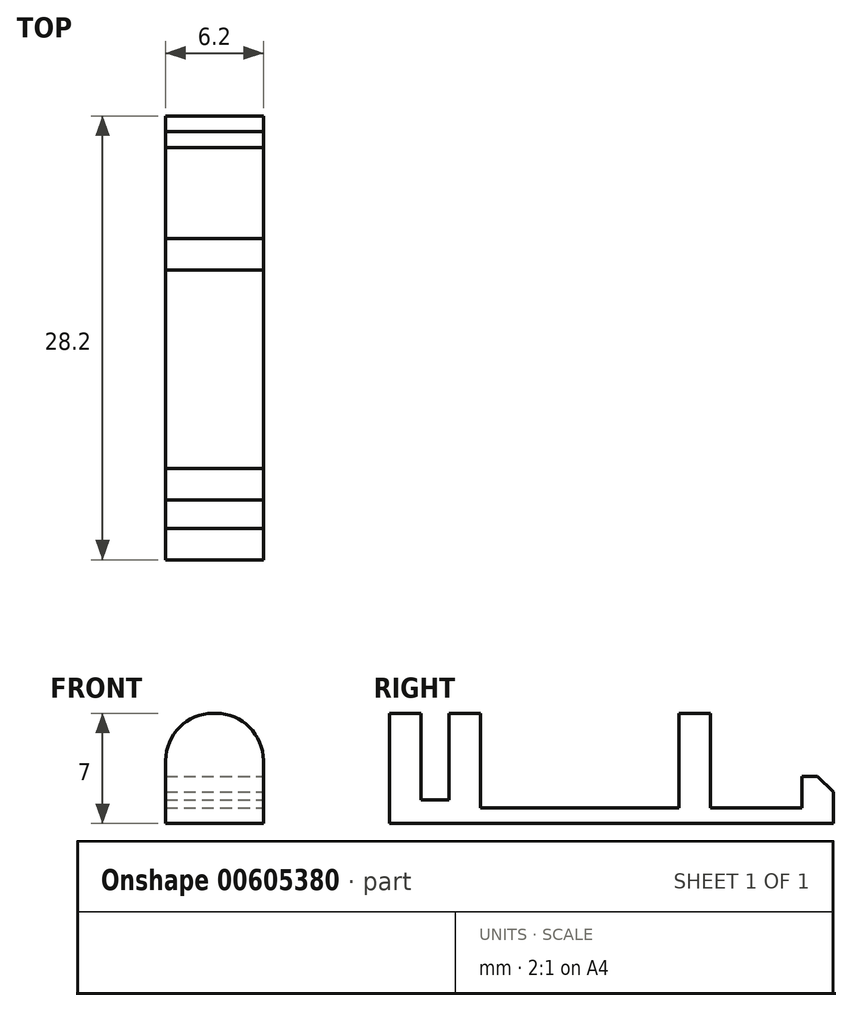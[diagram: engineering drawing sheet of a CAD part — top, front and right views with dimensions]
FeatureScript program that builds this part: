
annotation { "Feature Type Name" : "Feature", "Feature Type Description" : "" }
export const myFeature = defineFeature(function(context is Context, id is Id, definition is map)
    precondition{}
    {
        {
            var Q0;
            Q0=qCreatedBy(makeId("Top.planeOp"),FACE);
            var sketch = newSketch(context, id + "F0", { "sketchPlane" : qUnion([Q0])});
            skLineSegment(sketch, "E0.bottom", {"start": v(-3.1, 6.3) * mm, "end": v(3.1, 6.3) * mm});
            skLineSegment(sketch, "E0.top", {"start": v(-3.1, -6.3) * mm, "end": v(3.1, -6.3) * mm});
            skLineSegment(sketch, "E0.left", {"start": v(-3.1, 6.3) * mm, "end": v(-3.1, -6.3) * mm});
            skLineSegment(sketch, "E0.right", {"start": v(3.1, 6.3) * mm, "end": v(3.1, -6.3) * mm});
            skPoint(sketch, "E1", {"position": v(0, -6.3) * mm});
            skPoint(sketch, "E2", {"position": v(-3.1, 0) * mm});
            skLineSegment(sketch, "E3.top", {"start": v(-3.1, -8.3) * mm, "end": v(3.1, -8.3) * mm});
            skLineSegment(sketch, "E3.left", {"start": v(-3.1, -6.3) * mm, "end": v(-3.1, -8.3) * mm});
            skLineSegment(sketch, "E3.right", {"start": v(3.1, -6.3) * mm, "end": v(3.1, -8.3) * mm});
            skLineSegment(sketch, "E4.top", {"start": v(-3.1, -10.1) * mm, "end": v(3.1, -10.1) * mm});
            skLineSegment(sketch, "E4.left", {"start": v(-3.1, -8.3) * mm, "end": v(-3.1, -10.1) * mm});
            skLineSegment(sketch, "E4.right", {"start": v(3.1, -8.3) * mm, "end": v(3.1, -10.1) * mm});
            skLineSegment(sketch, "E5.top", {"start": v(-3.1, 8.3) * mm, "end": v(3.1, 8.3) * mm});
            skLineSegment(sketch, "E5.left", {"start": v(-3.1, 6.3) * mm, "end": v(-3.1, 8.3) * mm});
            skLineSegment(sketch, "E5.right", {"start": v(3.1, 6.3) * mm, "end": v(3.1, 8.3) * mm});
            skLineSegment(sketch, "E6.top", {"start": v(-3.1, 14.1) * mm, "end": v(3.1, 14.1) * mm});
            skLineSegment(sketch, "E6.left", {"start": v(-3.1, 8.3) * mm, "end": v(-3.1, 14.1) * mm});
            skLineSegment(sketch, "E6.right", {"start": v(3.1, 8.3) * mm, "end": v(3.1, 14.1) * mm});
            skLineSegment(sketch, "E7.top", {"start": v(-3.1, 16.1) * mm, "end": v(3.1, 16.1) * mm});
            skLineSegment(sketch, "E7.left", {"start": v(-3.1, 14.1) * mm, "end": v(-3.1, 16.1) * mm});
            skLineSegment(sketch, "E7.right", {"start": v(3.1, 14.1) * mm, "end": v(3.1, 16.1) * mm});
            skLineSegment(sketch, "E8.top", {"start": v(-3.1, -12.1) * mm, "end": v(3.1, -12.1) * mm});
            skLineSegment(sketch, "E8.left", {"start": v(-3.1, -10.1) * mm, "end": v(-3.1, -12.1) * mm});
            skLineSegment(sketch, "E8.right", {"start": v(3.1, -10.1) * mm, "end": v(3.1, -12.1) * mm});
            skSolve(sketch);
        }
        {
            var Q0;
            Q0=makeQuery(id+"F0.imprint","IMPRINT",FACE,{"disambiguationData":[TD([[makeQuery(id+"F0.imprint","IMPRINT",EDGE,{"derivedFrom":sQuery(id+"F0.wireOp",EDGE,"E6.top")}),1.0]])]});
            var Q1;
            Q1=makeQuery(id+"F0.imprint","IMPRINT",FACE,{"disambiguationData":[TD([[makeQuery(id+"F0.imprint","IMPRINT",EDGE,{"derivedFrom":sQuery(id+"F0.wireOp",EDGE,"E4.top")}),-1.0]])]});
            var Q2;
            Q2=makeQuery(id+"F0.imprint","IMPRINT",FACE,{"disambiguationData":[TD([[makeQuery(id+"F0.imprint","IMPRINT",EDGE,{"derivedFrom":sQuery(id+"F0.wireOp",EDGE,"E0.left")}),1.0]])]});
            var Q3;
            Q3=makeQuery(id+"F0.imprint","IMPRINT",FACE,{"disambiguationData":[TD([[makeQuery(id+"F0.imprint","IMPRINT",EDGE,{"derivedFrom":sQuery(id+"F0.wireOp",EDGE,"E0.top")}),-1.0]])]});
            var Q4;
            Q4=makeQuery(id+"F0.imprint","IMPRINT",FACE,{"disambiguationData":[TD([[makeQuery(id+"F0.imprint","IMPRINT",EDGE,{"derivedFrom":sQuery(id+"F0.wireOp",EDGE,"E3.top")}),-1.0]])]});
            var Q5;
            Q5=makeQuery(id+"F0.imprint","IMPRINT",FACE,{"disambiguationData":[TD([[makeQuery(id+"F0.imprint","IMPRINT",EDGE,{"derivedFrom":sQuery(id+"F0.wireOp",EDGE,"E0.bottom")}),1.0]])]});
            var Q6;
            Q6=makeQuery(id+"F0.imprint","IMPRINT",FACE,{"disambiguationData":[TD([[makeQuery(id+"F0.imprint","IMPRINT",EDGE,{"derivedFrom":sQuery(id+"F0.wireOp",EDGE,"E5.top")}),1.0]])]});
            extrude(context, id + "F1", {"entities" : qUnion([Q0, Q1, Q2, Q3, Q4, Q5, Q6]), "oppositeDirection" : true, "depth" : 1 * mm, "offsetDistance" : 25 * mm});
        }
        {
            var Q0;
            Q0=makeQuery(id+"F0.imprint","IMPRINT",FACE,{"disambiguationData":[TD([[makeQuery(id+"F0.imprint","IMPRINT",EDGE,{"derivedFrom":sQuery(id+"F0.wireOp",EDGE,"E0.bottom")}),1.0]])]});
            var Q1;
            Q1=makeQuery(id+"F0.imprint","IMPRINT",FACE,{"disambiguationData":[TD([[makeQuery(id+"F0.imprint","IMPRINT",EDGE,{"derivedFrom":sQuery(id+"F0.wireOp",EDGE,"E0.top")}),-1.0]])]});
            var Q2;
            Q2=makeQuery(id+"F0.imprint","IMPRINT",FACE,{"disambiguationData":[TD([[makeQuery(id+"F0.imprint","IMPRINT",EDGE,{"derivedFrom":sQuery(id+"F0.wireOp",EDGE,"E4.top")}),-1.0]])]});
            extrude(context, id + "F2", {"entities" : qUnion([Q0, Q1, Q2]), "operationType" : NewBodyOperationType.ADD, "depth" : 6 * mm, "offsetDistance" : 25 * mm});
        }
        {
            var Q0;
            Q0=makeQuery(id+"F2.opExtrude","CAP_EDGE",EDGE,{"disambiguationData":[OSD([sQuery(id+"F0.wireOp",EDGE,"E7.left")])],"isStart":false});
            var Q1;
            Q1=makeQuery(id+"F2.opExtrude","CAP_EDGE",EDGE,{"disambiguationData":[OSD([sQuery(id+"F0.wireOp",EDGE,"E5.left")])],"isStart":false});
            var Q2;
            Q2=makeQuery(id+"F2.opExtrude","CAP_EDGE",EDGE,{"disambiguationData":[OSD([sQuery(id+"F0.wireOp",EDGE,"E3.left")])],"isStart":false});
            var Q3;
            Q3=makeQuery(id+"F2.opExtrude","CAP_EDGE",EDGE,{"disambiguationData":[OSD([sQuery(id+"F0.wireOp",EDGE,"E8.left")])],"isStart":false});
            var Q4;
            Q4=makeQuery(id+"F2.opExtrude","CAP_EDGE",EDGE,{"disambiguationData":[OSD([sQuery(id+"F0.wireOp",EDGE,"E7.right")])],"isStart":false});
            var Q5;
            Q5=makeQuery(id+"F2.opExtrude","CAP_EDGE",EDGE,{"disambiguationData":[OSD([sQuery(id+"F0.wireOp",EDGE,"E5.right")])],"isStart":false});
            var Q6;
            Q6=makeQuery(id+"F2.opExtrude","CAP_EDGE",EDGE,{"disambiguationData":[OSD([sQuery(id+"F0.wireOp",EDGE,"E3.right")])],"isStart":false});
            var Q7;
            Q7=makeQuery(id+"F2.opExtrude","CAP_EDGE",EDGE,{"disambiguationData":[OSD([sQuery(id+"F0.wireOp",EDGE,"E8.right")])],"isStart":false});
            fillet(context, id + "F3", {"entities" : qUnion([Q0, Q1, Q2, Q3, Q4, Q5, Q6, Q7]), "radius" : 3 * mm, "tangentPropagation" : true, "allowEdgeOverflow" : false});
        }
        {
            var Q0;
            Q0=makeQuery(id+"F0.imprint","IMPRINT",FACE,{"disambiguationData":[TD([[makeQuery(id+"F0.imprint","IMPRINT",EDGE,{"derivedFrom":sQuery(id+"F0.wireOp",EDGE,"E3.top")}),-1.0]])]});
            extrude(context, id + "F4", {"entities" : qUnion([Q0]), "operationType" : NewBodyOperationType.ADD, "depth" : .5 * mm, "offsetDistance" : 25 * mm});
        }
        {
            var Q0;
            Q0=makeQuery(id+"F0.imprint","IMPRINT",FACE,{"disambiguationData":[TD([[makeQuery(id+"F0.imprint","IMPRINT",EDGE,{"derivedFrom":sQuery(id+"F0.wireOp",EDGE,"E6.top")}),1.0]])]});
            extrude(context, id + "F5", {"entities" : qUnion([Q0]), "operationType" : NewBodyOperationType.ADD, "depth" : 2 * mm, "offsetDistance" : 25 * mm});
        }
        {
            var Q0;
            Q0=makeQuery(id+"F5.opExtrude","CAP_EDGE",EDGE,{"disambiguationData":[OSD([sQuery(id+"F0.wireOp",EDGE,"E7.top")])],"isStart":false});
            chamfer(context, id + "F6", {"entities" : qUnion([Q0]), "width" : 1 * mm, "tangentPropagation" : true});
        }
    });
